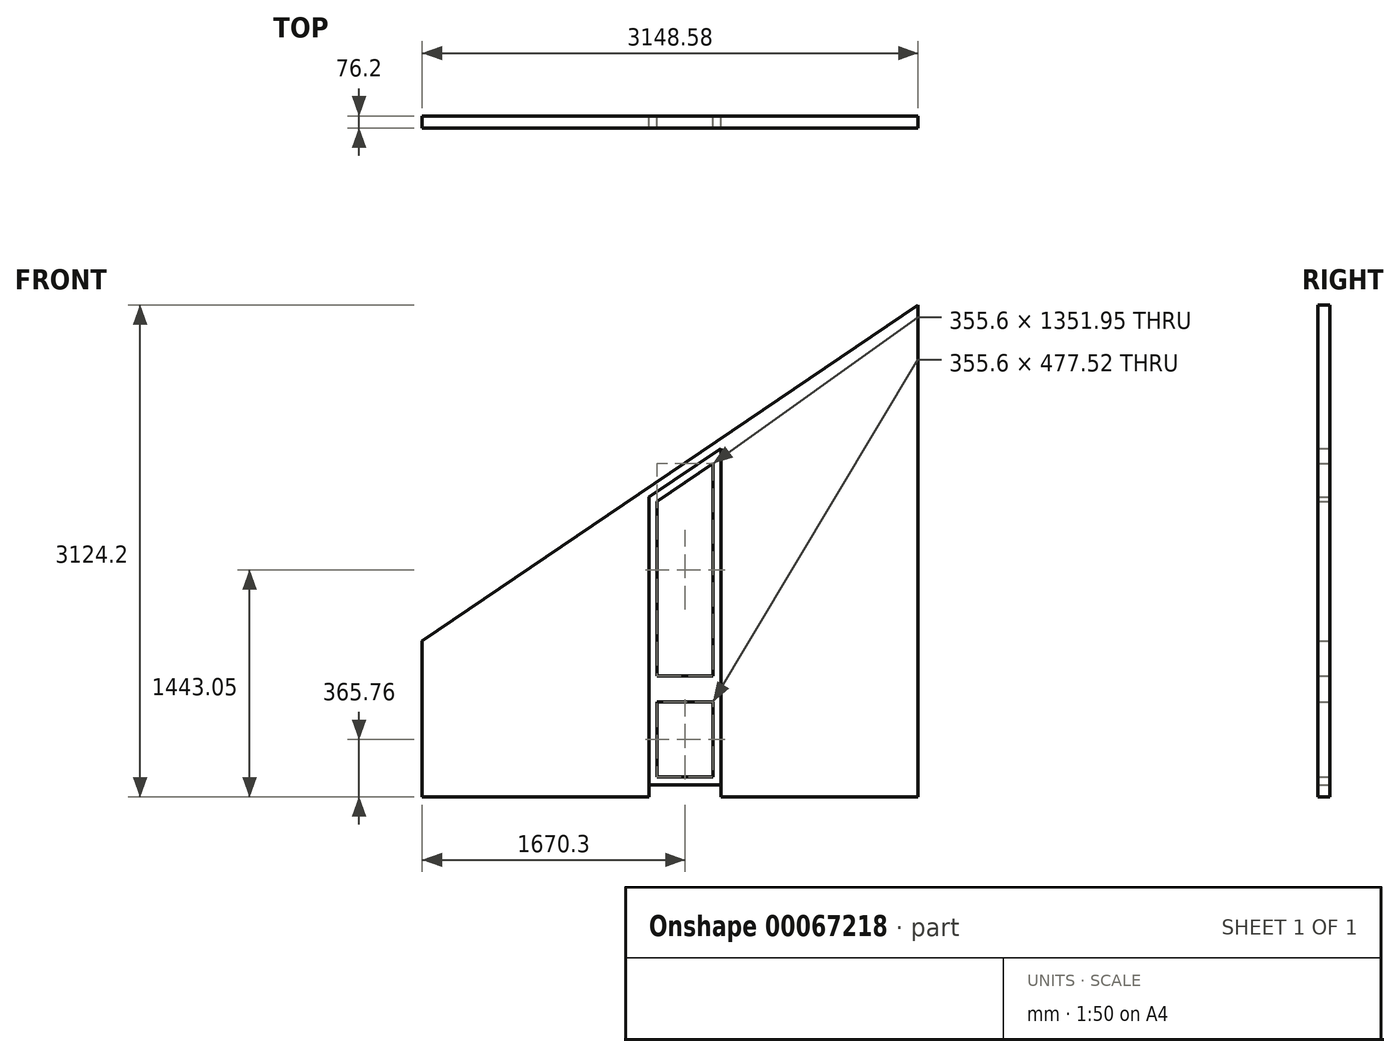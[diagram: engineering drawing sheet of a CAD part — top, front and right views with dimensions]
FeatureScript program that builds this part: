
annotation { "Feature Type Name" : "Feature", "Feature Type Description" : "" }
export const myFeature = defineFeature(function(context is Context, id is Id, definition is map)
    precondition{}
    {
        {
            var Q0;
            Q0=qCreatedBy(makeId("Front.planeOp"),FACE);
            var sketch = newSketch(context, id + "F0", { "sketchPlane" : qUnion([Q0])});
            skLineSegment(sketch, "E0", {"start": v(0, 0) * mm, "end": v(-3148.58, 0) * mm});
            skLineSegment(sketch, "E1", {"start": v(-3148.58, 0) * mm, "end": v(-3148.58, 990.6) * mm});
            skLineSegment(sketch, "E2", {"start": v(-3148.58, 990.6) * mm, "end": v(0, 3124.2) * mm});
            skLineSegment(sketch, "E3", {"start": v(0, 3124.2) * mm, "end": v(0, 0) * mm});
            skLineSegment(sketch, "E4.bottom", {"start": v(-1706.88, 0) * mm, "end": v(-1249.68, 0) * mm});
            skLineSegment(sketch, "E4.left", {"start": v(-1706.88, 0) * mm, "end": v(-1706.88, 1905) * mm});
            skLineSegment(sketch, "E4.right", {"start": v(-1249.68, 0) * mm, "end": v(-1249.68, 2214.82) * mm});
            skLineSegment(sketch, "E5", {"start": v(-1706.88, 1905) * mm, "end": v(-1249.68, 2214.82) * mm});
            skLineSegment(sketch, "E6", {"start": v(-1706.88, 76.2) * mm, "end": v(-1249.68, 76.2) * mm});
            skLineSegment(sketch, "E7", {"start": v(-1706.88, 655.32) * mm, "end": v(-1249.68, 655.32) * mm});
            skLineSegment(sketch, "E8", {"start": v(-1706.88, 716.28) * mm, "end": v(-1249.68, 716.28) * mm});
            skLineSegment(sketch, "E9", {"start": v(-1656.08, 604.52) * mm, "end": v(-1656.08, 127) * mm});
            skLineSegment(sketch, "E10", {"start": v(-1656.08, 127) * mm, "end": v(-1300.48, 127) * mm});
            skLineSegment(sketch, "E11", {"start": v(-1300.48, 127) * mm, "end": v(-1300.48, 604.52) * mm});
            skLineSegment(sketch, "E12", {"start": v(-1300.48, 604.52) * mm, "end": v(-1656.08, 604.52) * mm});
            skLineSegment(sketch, "E13", {"start": v(-1656.08, 767.08) * mm, "end": v(-1656.08, 1878.06) * mm});
            skLineSegment(sketch, "E14", {"start": v(-1656.08, 1878.06) * mm, "end": v(-1300.48, 2119.03) * mm});
            skLineSegment(sketch, "E15", {"start": v(-1300.48, 2119.03) * mm, "end": v(-1300.48, 767.08) * mm});
            skLineSegment(sketch, "E16", {"start": v(-1300.48, 767.08) * mm, "end": v(-1656.08, 767.08) * mm});
            skSolve(sketch);
        }
        {
            var Q0;
            {var subQ13=sQuery(id+"F0.wireOp",EDGE,"E1");Q0=makeQuery(id+"F0.imprint","IMPRINT",FACE,{"disambiguationData":[TD([[makeQuery(id+"F0.imprint","IMPRINT",EDGE,{"derivedFrom":subQ13}),-1.0]])]});}
            var Q1;
            {var subQ0=sQuery(id+"F0.wireOp",EDGE,"E4.bottom");Q1=makeQuery(id+"F0.imprint","IMPRINT",FACE,{"disambiguationData":[TD([[makeQuery(id+"F0.imprint","IMPRINT",EDGE,{"derivedFrom":subQ0}),1.0]])]});}
            extrude(context, id + "F1", {"entities" : qUnion([Q0, Q1]), "depth" : 76.2 * mm});
        }
        {
            var Q0;
            Q0=makeQuery(id+"F0.imprint","IMPRINT",FACE,{"disambiguationData":[TD([[makeQuery(id+"F0.imprint","IMPRINT",EDGE,{"derivedFrom":sQuery(id+"F0.wireOp",EDGE,"E0")}),-1.0]])]});
            var sketch = newSketch(context, id + "F2", { "sketchPlane" : qUnion([Q0])});
            skLineSegment(sketch, "E17", {"start": v(-3148.58, 806.5) * mm, "end": v(0, 2940.1) * mm});
            skLineSegment(sketch, "E18", {"start": v(0, 2940.1) * mm, "end": v(85.5, 2998.04) * mm});
            skLineSegment(sketch, "E19", {"start": v(0, 3124.2) * mm, "end": v(85.5, 2998.04) * mm, "construction": true});
            skLineSegment(sketch, "E20", {"start": v(-3148.58, 990.6) * mm, "end": v(-2688.56, 311.73) * mm, "construction": true});
            skLineSegment(sketch, "E21", {"start": v(-3148.58, 0) * mm, "end": v(0, 2133.6) * mm, "construction": true});
            skLineSegment(sketch, "E22.bottom", {"start": v(0, 2940.1) * mm, "end": v(-3263.14, 728.88) * mm});
            skLineSegment(sketch, "E22.top", {"start": v(114.56, 2771.05) * mm, "end": v(-3148.58, 559.82) * mm});
            skLineSegment(sketch, "E22.left", {"start": v(0, 2940.1) * mm, "end": v(114.56, 2771.05) * mm});
            skLineSegment(sketch, "E22.right", {"start": v(-3263.14, 728.88) * mm, "end": v(-3148.58, 559.82) * mm});
            skLineSegment(sketch, "E23.bottom", {"start": v(-3263.14, 482.19) * mm, "end": v(0, 2693.42) * mm});
            skLineSegment(sketch, "E23.top", {"start": v(-3148.58, 313.13) * mm, "end": v(114.56, 2524.36) * mm});
            skLineSegment(sketch, "E23.left", {"start": v(-3263.14, 482.19) * mm, "end": v(-3148.58, 313.13) * mm});
            skLineSegment(sketch, "E23.right", {"start": v(0, 2693.42) * mm, "end": v(114.56, 2524.36) * mm});
            skLineSegment(sketch, "E24.right", {"start": v(0, 2446.73) * mm, "end": v(114.56, 2277.67) * mm});
            skLineSegment(sketch, "E24.left", {"start": v(-3263.14, 235.5) * mm, "end": v(-3148.58, 66.44) * mm});
            skLineSegment(sketch, "E24.top", {"start": v(-3148.58, 66.44) * mm, "end": v(114.56, 2277.67) * mm});
            skLineSegment(sketch, "E24.bottom", {"start": v(-3263.14, 235.5) * mm, "end": v(0, 2446.73) * mm});
            skLineSegment(sketch, "E25.right", {"start": v(0, 2200.04) * mm, "end": v(114.56, 2030.99) * mm});
            skLineSegment(sketch, "E25.left", {"start": v(-3216.57, 20.38) * mm, "end": v(-3102, -148.68) * mm});
            skLineSegment(sketch, "E25.top", {"start": v(-3102, -148.68) * mm, "end": v(114.56, 2030.99) * mm});
            skLineSegment(sketch, "E25.bottom", {"start": v(-3216.57, 20.38) * mm, "end": v(0, 2200.04) * mm});
            skLineSegment(sketch, "E26.right", {"start": v(0, 1953.36) * mm, "end": v(114.56, 1784.3) * mm});
            skLineSegment(sketch, "E26.left", {"start": v(-3027.89, -98.45) * mm, "end": v(-2913.33, -267.51) * mm});
            skLineSegment(sketch, "E26.top", {"start": v(-2913.33, -267.51) * mm, "end": v(114.56, 1784.3) * mm});
            skLineSegment(sketch, "E26.bottom", {"start": v(-3027.89, -98.45) * mm, "end": v(0, 1953.36) * mm});
            skLineSegment(sketch, "E27.right", {"start": v(-6.9, 1702) * mm, "end": v(107.66, 1532.94) * mm});
            skLineSegment(sketch, "E27.left", {"start": v(-2530.14, -7.85) * mm, "end": v(-2415.58, -176.9) * mm});
            skLineSegment(sketch, "E27.top", {"start": v(-2415.58, -176.9) * mm, "end": v(107.66, 1532.94) * mm});
            skLineSegment(sketch, "E27.bottom", {"start": v(-2530.14, -7.85) * mm, "end": v(-6.9, 1702) * mm});
            skLineSegment(sketch, "E28.right", {"start": v(23.12, 1475.65) * mm, "end": v(137.68, 1306.6) * mm});
            skLineSegment(sketch, "E28.left", {"start": v(-2247.8, -63.2) * mm, "end": v(-2133.23, -232.26) * mm});
            skLineSegment(sketch, "E28.top", {"start": v(-2133.23, -232.26) * mm, "end": v(137.68, 1306.6) * mm});
            skLineSegment(sketch, "E28.bottom", {"start": v(-2247.8, -63.2) * mm, "end": v(23.12, 1475.65) * mm});
            skLineSegment(sketch, "E29.right", {"start": v(75.7, 1264.6) * mm, "end": v(190.26, 1095.54) * mm});
            skLineSegment(sketch, "E29.left", {"start": v(-1438.25, 238.69) * mm, "end": v(-1323.69, 69.63) * mm});
            skLineSegment(sketch, "E29.top", {"start": v(-1323.69, 69.63) * mm, "end": v(190.26, 1095.54) * mm});
            skLineSegment(sketch, "E29.bottom", {"start": v(-1438.25, 238.69) * mm, "end": v(75.7, 1264.6) * mm});
            skLineSegment(sketch, "E30.right", {"start": v(37.9, 992.3) * mm, "end": v(152.46, 823.24) * mm});
            skLineSegment(sketch, "E30.left", {"start": v(-1349, 52.48) * mm, "end": v(-1234.44, -116.58) * mm});
            skLineSegment(sketch, "E30.top", {"start": v(-1234.44, -116.58) * mm, "end": v(152.46, 823.24) * mm});
            skLineSegment(sketch, "E30.bottom", {"start": v(-1349, 52.48) * mm, "end": v(37.9, 992.3) * mm});
            skLineSegment(sketch, "E31.right", {"start": v(38.35, 745.9) * mm, "end": v(152.9, 576.85) * mm});
            skLineSegment(sketch, "E31.left", {"start": v(-1068.57, -4.18) * mm, "end": v(-954, -173.24) * mm});
            skLineSegment(sketch, "E31.top", {"start": v(-954, -173.24) * mm, "end": v(152.9, 576.85) * mm});
            skLineSegment(sketch, "E31.bottom", {"start": v(-1068.57, -4.18) * mm, "end": v(38.35, 745.9) * mm});
            skLineSegment(sketch, "E32.right", {"start": v(49.05, 506.47) * mm, "end": v(163.6, 337.41) * mm});
            skLineSegment(sketch, "E32.left", {"start": v(-698.36, 0) * mm, "end": v(-583.8, -169.06) * mm});
            skLineSegment(sketch, "E32.top", {"start": v(-583.8, -169.06) * mm, "end": v(163.6, 337.41) * mm});
            skLineSegment(sketch, "E32.bottom", {"start": v(-698.36, 0) * mm, "end": v(49.05, 506.47) * mm});
            skLineSegment(sketch, "E33.right", {"start": v(80.25, 280.93) * mm, "end": v(194.81, 111.87) * mm});
            skLineSegment(sketch, "E33.left", {"start": v(-334.32, 0) * mm, "end": v(-219.76, -169.06) * mm});
            skLineSegment(sketch, "E33.top", {"start": v(-219.76, -169.06) * mm, "end": v(194.81, 111.87) * mm});
            skLineSegment(sketch, "E33.bottom", {"start": v(-334.32, 0) * mm, "end": v(80.25, 280.93) * mm});
            skLineSegment(sketch, "E34", {"start": v(-3148.58, 806.5) * mm, "end": v(-3233, 931.08) * mm});
            skLineSegment(sketch, "E35", {"start": v(-3233, 931.08) * mm, "end": v(0, 3124.2) * mm});
            skLineSegment(sketch, "E36", {"start": v(-1517.01, 1665.43) * mm, "end": v(-1402.45, 1496.38) * mm});
            skLineSegment(sketch, "E37", {"start": v(-1402.45, 1496.38) * mm, "end": v(-1517.01, 1418.75) * mm});
            skLineSegment(sketch, "E38", {"start": v(-1517.01, 1418.75) * mm, "end": v(-1402.45, 1249.69) * mm});
            skSolve(sketch);
        }
        {
            var Q0;
            {var subQ1=sQuery(id+"F0.wireOp",EDGE,"E5");Q0=makeQuery(id+"F0.imprint","IMPRINT",FACE,{"disambiguationData":[TD([[makeQuery(id+"F0.imprint","IMPRINT",EDGE,{"derivedFrom":subQ1}),-1.0]])]});}
            var Q1;
            {var subQ1=sQuery(id+"F0.wireOp",EDGE,"E6");Q1=makeQuery(id+"F0.imprint","IMPRINT",FACE,{"disambiguationData":[TD([[makeQuery(id+"F0.imprint","IMPRINT",EDGE,{"derivedFrom":subQ1}),1.0]])]});}
            var Q2;
            {var subQ0=sQuery(id+"F0.wireOp",EDGE,"E7");Q2=makeQuery(id+"F0.imprint","IMPRINT",FACE,{"disambiguationData":[TD([[makeQuery(id+"F0.imprint","IMPRINT",EDGE,{"derivedFrom":subQ0}),1.0]])]});}
            extrude(context, id + "F3", {"entities" : qUnion([Q0, Q1, Q2]), "depth" : 76.2 * mm});
        }
    });
